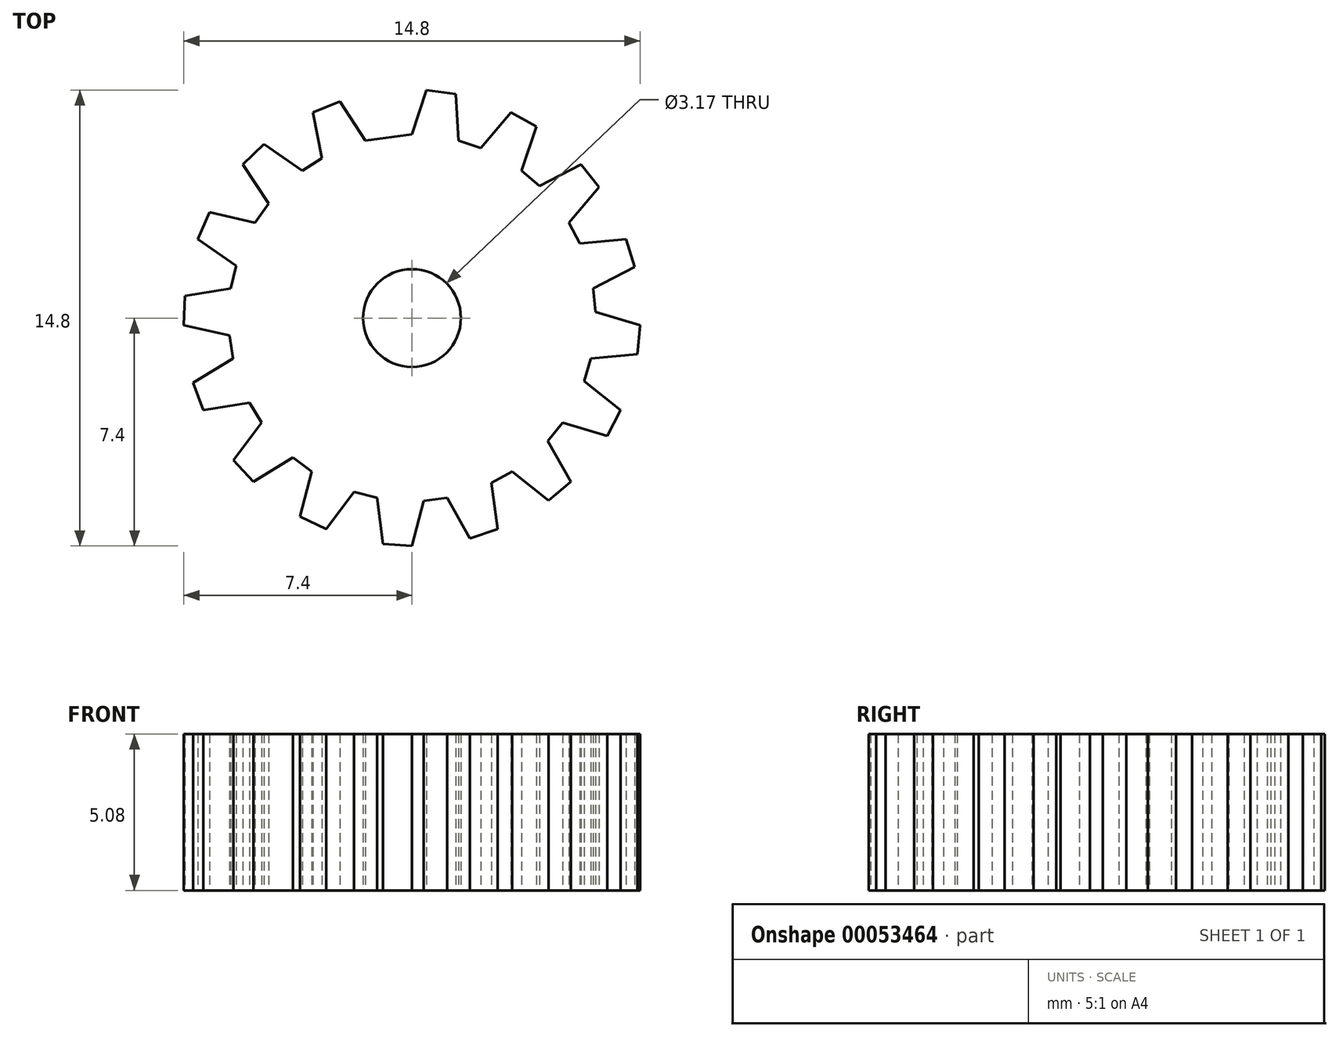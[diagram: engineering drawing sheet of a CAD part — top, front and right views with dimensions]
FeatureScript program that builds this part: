
annotation { "Feature Type Name" : "Feature", "Feature Type Description" : "" }
export const myFeature = defineFeature(function(context is Context, id is Id, definition is map)
    precondition{}
    {
        {
            var Q0;
            Q0=qCreatedBy(makeId("Top.planeOp"),FACE);
            var sketch = newSketch(context, id + "F0", { "sketchPlane" : qUnion([Q0])});
            skLineSegment(sketch, "E0", {"start": v(0, 5.96) * mm, "end": v(0.47, 7.4) * mm});
            skLineSegment(sketch, "E1", {"start": v(0.47, 7.4) * mm, "end": v(1.42, 7.28) * mm});
            skLineSegment(sketch, "E2", {"start": v(1.42, 7.28) * mm, "end": v(1.5, 5.77) * mm});
            skLineSegment(sketch, "E3", {"start": v(2.23, 5.52) * mm, "end": v(3.21, 6.68) * mm});
            skLineSegment(sketch, "E4", {"start": v(3.21, 6.68) * mm, "end": v(4.04, 6.21) * mm});
            skLineSegment(sketch, "E5", {"start": v(4.04, 6.21) * mm, "end": v(3.56, 4.78) * mm});
            skLineSegment(sketch, "E6", {"start": v(3.56, 4.78) * mm, "end": v(4.14, 4.28) * mm});
            skLineSegment(sketch, "E7", {"start": v(4.14, 4.28) * mm, "end": v(5.48, 4.99) * mm});
            skLineSegment(sketch, "E8", {"start": v(5.48, 4.99) * mm, "end": v(6.07, 4.24) * mm});
            skLineSegment(sketch, "E9", {"start": v(6.07, 4.24) * mm, "end": v(5.1, 3.1) * mm});
            skLineSegment(sketch, "E10", {"start": v(5.1, 3.1) * mm, "end": v(5.44, 2.42) * mm});
            skLineSegment(sketch, "E11", {"start": v(5.44, 2.42) * mm, "end": v(6.95, 2.57) * mm});
            skLineSegment(sketch, "E12", {"start": v(6.95, 2.57) * mm, "end": v(7.22, 1.66) * mm});
            skLineSegment(sketch, "E13", {"start": v(7.22, 1.66) * mm, "end": v(5.88, 0.96) * mm});
            skLineSegment(sketch, "E14", {"start": v(5.88, 0.96) * mm, "end": v(5.95, 0.2) * mm});
            skLineSegment(sketch, "E15", {"start": v(5.95, 0.2) * mm, "end": v(7.4, -0.23) * mm});
            skLineSegment(sketch, "E16", {"start": v(7.4, -0.23) * mm, "end": v(7.31, -1.17) * mm});
            skLineSegment(sketch, "E17", {"start": v(7.31, -1.17) * mm, "end": v(5.8, -1.32) * mm});
            skLineSegment(sketch, "E18", {"start": v(5.8, -1.32) * mm, "end": v(5.59, -2.05) * mm});
            skLineSegment(sketch, "E19", {"start": v(5.59, -2.05) * mm, "end": v(6.77, -2.99) * mm});
            skLineSegment(sketch, "E20", {"start": v(6.77, -2.99) * mm, "end": v(6.33, -3.83) * mm});
            skLineSegment(sketch, "E21", {"start": v(6.33, -3.83) * mm, "end": v(4.88, -3.4) * mm});
            skLineSegment(sketch, "E22", {"start": v(4.88, -3.4) * mm, "end": v(4.4, -4) * mm});
            skLineSegment(sketch, "E23", {"start": v(4.4, -4) * mm, "end": v(5.15, -5.31) * mm});
            skLineSegment(sketch, "E24", {"start": v(5.15, -5.31) * mm, "end": v(4.43, -5.93) * mm});
            skLineSegment(sketch, "E25", {"start": v(4.43, -5.93) * mm, "end": v(3.25, -4.98) * mm});
            skLineSegment(sketch, "E26", {"start": v(3.25, -4.98) * mm, "end": v(2.58, -5.36) * mm});
            skLineSegment(sketch, "E27", {"start": v(2.58, -5.36) * mm, "end": v(2.78, -6.86) * mm});
            skLineSegment(sketch, "E28", {"start": v(2.78, -6.86) * mm, "end": v(1.88, -7.16) * mm});
            skLineSegment(sketch, "E29", {"start": v(1.88, -7.16) * mm, "end": v(1.14, -5.83) * mm});
            skLineSegment(sketch, "E30", {"start": v(1.14, -5.83) * mm, "end": v(0.38, -5.93) * mm});
            skLineSegment(sketch, "E31", {"start": v(0.38, -5.93) * mm, "end": v(0, -7.4) * mm});
            skLineSegment(sketch, "E32", {"start": v(0, -7.4) * mm, "end": v(-0.95, -7.34) * mm});
            skLineSegment(sketch, "E33", {"start": v(-0.95, -7.34) * mm, "end": v(-1.14, -5.83) * mm});
            skLineSegment(sketch, "E34", {"start": v(-1.14, -5.83) * mm, "end": v(-1.88, -5.64) * mm});
            skLineSegment(sketch, "E35", {"start": v(-1.88, -5.64) * mm, "end": v(-2.78, -6.86) * mm});
            skLineSegment(sketch, "E36", {"start": v(-2.78, -6.86) * mm, "end": v(-3.63, -6.44) * mm});
            skLineSegment(sketch, "E37", {"start": v(-3.63, -6.44) * mm, "end": v(-3.25, -4.98) * mm});
            skLineSegment(sketch, "E38", {"start": v(-3.25, -4.98) * mm, "end": v(-3.86, -4.52) * mm});
            skLineSegment(sketch, "E39", {"start": v(-3.86, -4.52) * mm, "end": v(-5.15, -5.31) * mm});
            skLineSegment(sketch, "E40", {"start": v(-5.15, -5.31) * mm, "end": v(-5.79, -4.6) * mm});
            skLineSegment(sketch, "E41", {"start": v(-5.79, -4.6) * mm, "end": v(-4.88, -3.4) * mm});
            skLineSegment(sketch, "E42", {"start": v(-4.88, -3.4) * mm, "end": v(-5.28, -2.75) * mm});
            skLineSegment(sketch, "E43", {"start": v(-5.28, -2.75) * mm, "end": v(-6.77, -2.99) * mm});
            skLineSegment(sketch, "E44", {"start": v(-6.77, -2.99) * mm, "end": v(-7.1, -2.1) * mm});
            skLineSegment(sketch, "E45", {"start": v(-7.1, -2.1) * mm, "end": v(-5.8, -1.32) * mm});
            skLineSegment(sketch, "E46", {"start": v(-5.8, -1.32) * mm, "end": v(-5.92, -0.56) * mm});
            skLineSegment(sketch, "E47", {"start": v(-5.92, -0.56) * mm, "end": v(-7.4, -0.23) * mm});
            skLineSegment(sketch, "E48", {"start": v(-7.4, -0.23) * mm, "end": v(-7.37, 0.72) * mm});
            skLineSegment(sketch, "E49", {"start": v(-7.37, 0.72) * mm, "end": v(-5.88, 0.96) * mm});
            skLineSegment(sketch, "E50", {"start": v(-5.88, 0.96) * mm, "end": v(-5.7, 1.7) * mm});
            skLineSegment(sketch, "E51", {"start": v(-5.7, 1.7) * mm, "end": v(-6.95, 2.57) * mm});
            skLineSegment(sketch, "E52", {"start": v(-6.95, 2.57) * mm, "end": v(-6.57, 3.43) * mm});
            skLineSegment(sketch, "E53", {"start": v(-6.57, 3.43) * mm, "end": v(-5.1, 3.1) * mm});
            skLineSegment(sketch, "E54", {"start": v(-5.1, 3.1) * mm, "end": v(-4.65, 3.72) * mm});
            skLineSegment(sketch, "E55", {"start": v(-4.65, 3.72) * mm, "end": v(-5.48, 4.99) * mm});
            skLineSegment(sketch, "E56", {"start": v(-5.48, 4.99) * mm, "end": v(-4.8, 5.65) * mm});
            skLineSegment(sketch, "E57", {"start": v(-4.8, 5.65) * mm, "end": v(-3.56, 4.78) * mm});
            skLineSegment(sketch, "E58", {"start": v(-2.92, 5.2) * mm, "end": v(-3.21, 6.68) * mm});
            skLineSegment(sketch, "E59", {"start": v(-3.21, 6.68) * mm, "end": v(-2.33, 7.04) * mm});
            skLineSegment(sketch, "E60", {"start": v(-2.33, 7.04) * mm, "end": v(-1.5, 5.77) * mm});
            skLineSegment(sketch, "E61", {"start": v(-3.56, 4.78) * mm, "end": v(-2.92, 5.2) * mm});
            skLineSegment(sketch, "E62", {"start": v(-1.5, 5.77) * mm, "end": v(0, 5.96) * mm});
            skLineSegment(sketch, "E63", {"start": v(1.5, 5.77) * mm, "end": v(2.23, 5.52) * mm});
            skCircle(sketch, "E64", {"center": v(0, 0) * mm, "radius": 1.59 * mm});
            skSolve(sketch);
        }
        {
            var Q0;
            Q0 = qSketchRegion(id + "F0", true);
            extrude(context, id + "F1", {"entities" : qUnion([Q0]), "depth" : 5.08 * mm});
        }
    });
